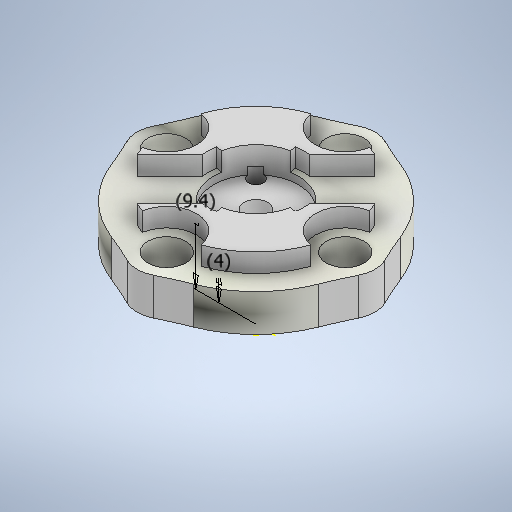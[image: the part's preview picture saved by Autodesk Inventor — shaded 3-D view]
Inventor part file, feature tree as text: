
AUTODESK INVENTOR PART (.ipt)
format: ipt  version: 2025.2 (Build 292293000, 293)  size: 946,176 bytes
history: native  units: in
note: dims shown in document units (in); Inventor stores cm internally (conversion verified against a paired STEP export)
features: sketch x21, extrude x19, fillet x2, projected_geometry x2, other x1
ambient origin geometry x8: Origin, YZ Plane, XZ Plane, XY Plane, X Axis, Y Axis, Z Axis, Center Point
bodies: Solid1 (feature_tree)
feature tree (45):
  extrude  "Extrusion1"  Depth=0.4094in TaperAngle=0.0deg
  extrude  "Extrusion2"  Depth=0.1181in
  extrude  "Extrusion3"  Depth=1.5748in TaperAngle=360.0deg
  extrude  "Extrusion5"  Depth=0.1969in
  extrude  "Extrusion6"  Depth=0.1437in
  extrude  "Extrusion8"  Depth=0.315in
  extrude  "Extrusion9"  Depth=0.315in
  extrude  "Extrusion10"  Depth=0.1575in
  extrude  "Extrusion11"  Depth=0.0984in
  fillet  "Fillet5"  Radius=0.2362in
  extrude  "Extrusion12"  Depth=0.3937in
  extrude  "Extrusion13"  Depth=0.2953in
  extrude  "Extrusion14"  Depth=0.3937in TaperAngle=0.0deg
  fillet  "Fillet7"  Radius=0.3937in
  extrude  "Extrusion15"  Depth=0.2559in TaperAngle=0.0deg
  sketch  "Sketch17"  dims[d63=0.2953in d64=0.1083in]
  extrude  "Extrusion16"  Depth=0.2362in TaperAngle=0.0deg
  extrude  "Extrusion17"  Depth=0.2953in
  extrude  "Extrusion18"  Depth=0.5118in
  extrude  "Extrusion19"  TaperAngle=135.0deg  [1 undecoded]
  extrude  "Extrusion20"  Depth=0.3937in TaperAngle=0.0deg
  extrude  "Extrusion21"  Depth=2.1412in
  sketch  "Sketch1"  dims[d0=0.1988in d1=0.4094in d2=0.0in]
  sketch  "Sketch2"  dims[d5=0.2008in d6=1.5748in d8=360.0deg]
  sketch  "Sketch Circular Pattern1"  dims[d3=0.9449in d4=0.1181in]
  sketch  "Sketch3"  dims[d10=0.1969in d11=0.0in d13=0.0827in]
  sketch  "Sketch5"  dims[d14=0.7219in d15=0.0in d19=0.1437in]
  sketch  "Sketch6"  dims[d20=0.4882in d21=0.0in d22=0.315in]
  sketch  "Sketch8"  dims[d23=0.315in d24=0.315in]
  sketch  "Sketch9"  dims[d25=0.315in d26=0.1575in]
  sketch  "Sketch10"  dims[d27=0.0984in d28=0.0in d30=0.189in d31=0.2362in]
  sketch  "Sketch11"  dims[d43=0.3937in d44=0.0in d45=0.3445in]
  sketch  "Sketch12"  dims[d46=135.0deg d47=0.2953in]
  projected_geometry  "Projected Loop1"
  sketch  "Sketch13"  dims[d51=135.0deg d52=0.2362in d53=0.0in d54=0.3937in d55=0.0in]
  sketch  "Sketch15"  dims[d56=0.2559in d57=0.2126in d58=0.0in]
  sketch  "Sketch16"  dims[d60=0.2037in d61=0.2362in d62=0.0in]
  sketch  "Sketch18"  dims[d65=0.1083in d66=0.5118in]
  sketch  "Sketch19"  dims[d67=0.1575in d68=135.0deg]
  sketch  "Sketch21"  dims[d69=0.315in d70=0.3937in d71=0.0in]
  projected_geometry  "Projected Loop2"
  sketch  "Sketch22"  dims[d73=0.0394in d74=0.0in d75=2.1412in]
  sketch  "Sketch23"  dims[d76=0.4488in]
  sketch  "Sketch24"  dims[d77=135.0deg d78=1.1681in d79=0.6871in d80=0.3937in d81=0.0in d82=0.3701in d83=0.1575in d84=0.3563in d85=0.0in d86=0.3937in d87=135.0deg d88=0.0787in d89=0.0787in d90=0.3937in d91=0.0in d92=0.3937in d93=0.0in d94=0.0394in d95=0.0in d96=0.126in d97=0.2338in d98=0.0in d99=0.2264in d100=0.0787in d101=0.0in]
  other  "Finish1"
note: 1 required parameter value undecoded (feature->parameter linkage not recoverable at this tier; creation-order binding heuristic only, values carry confidence <= 0.55)
